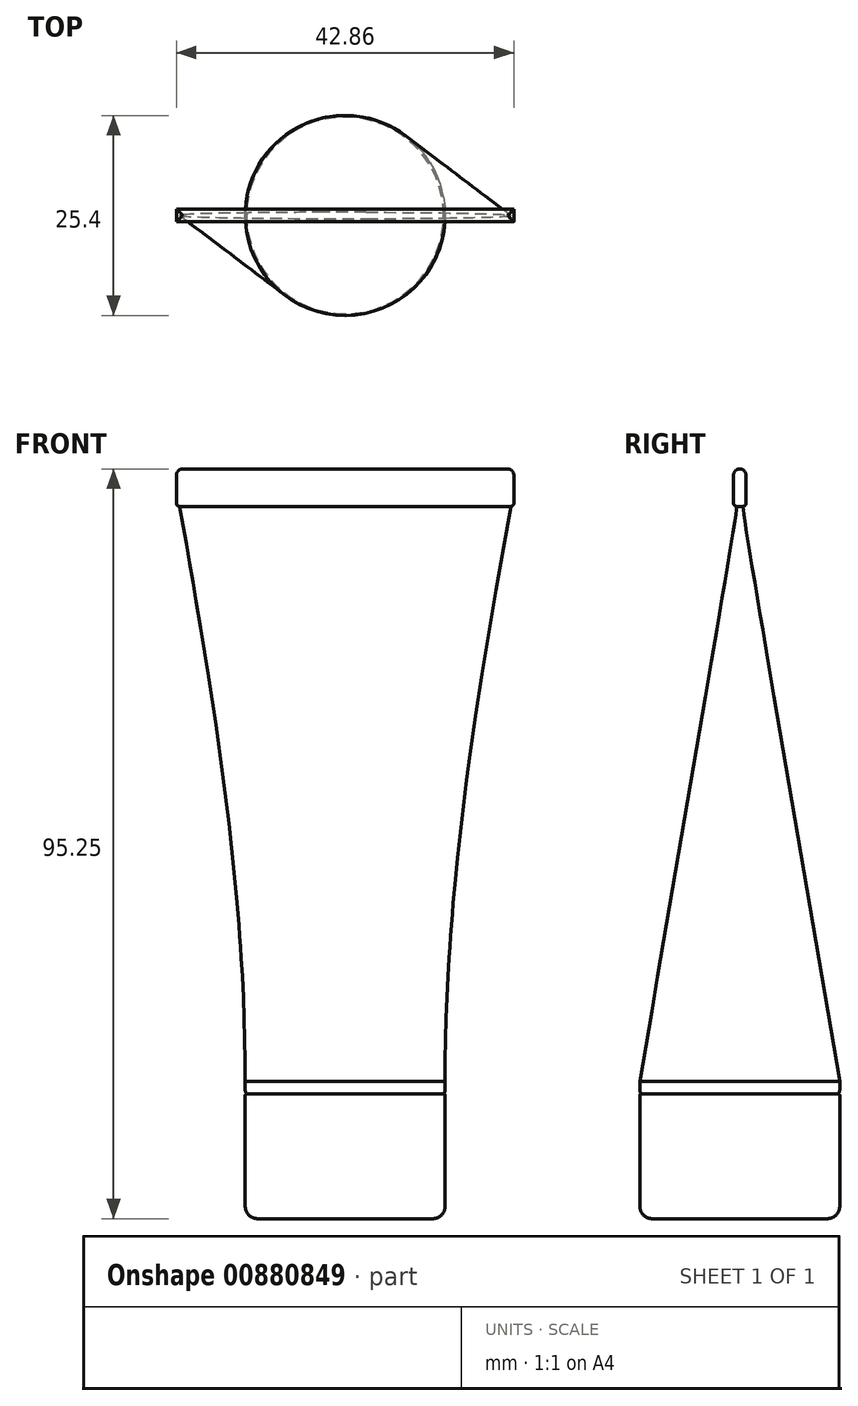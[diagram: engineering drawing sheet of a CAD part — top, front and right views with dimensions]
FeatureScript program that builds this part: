
annotation { "Feature Type Name" : "Feature", "Feature Type Description" : "" }
export const myFeature = defineFeature(function(context is Context, id is Id, definition is map)
    precondition{}
    {
        {
            var Q0;
            Q0=qCreatedBy(makeId("Front.planeOp"),FACE);
            var sketch = newSketch(context, id + "F0", { "sketchPlane" : qUnion([Q0])});
            skLineSegment(sketch, "E0", {"start": v(0, 0) * mm, "end": v(-11.11, 0) * mm});
            skArc(sketch, "E1", {"start": v(-11.11, 0) * mm, "mid": v(-12.24, 0.46) * mm, "end": v(-12.7, 1.59) * mm});
            skLineSegment(sketch, "E2", {"start": v(-12.7, 1.59) * mm, "end": v(-12.7, 15.63) * mm});
            skLineSegment(sketch, "E3", {"start": v(-12.7, 16.4) * mm, "end": v(-12.7, 17.46) * mm});
            skLineSegment(sketch, "E4", {"start": v(-12.7, 17.46) * mm, "end": v(0, 17.46) * mm});
            skLineSegment(sketch, "E5", {"start": v(0, 17.46) * mm, "end": v(0, 0) * mm});
            skArc(sketch, "E6.filletArc", {"start": v(-12.7, 16.4) * mm, "mid": v(-12.65, 16.12) * mm, "end": v(-12.5, 15.88) * mm});
            skArc(sketch, "E7.filletArc", {"start": v(-12.5, 15.88) * mm, "mid": v(-12.64, 15.79) * mm, "end": v(-12.7, 15.63) * mm});
            skSolve(sketch);
        }
        {
            var Q0;
            Q0=makeQuery(id+"F0.imprint","IMPRINT",FACE,{"disambiguationData":[TD([[makeQuery(id+"F0.imprint","IMPRINT",EDGE,{"derivedFrom":sQuery(id+"F0.wireOp",EDGE,"E0")}),-1.0]])]});
            var Q1;
            Q1=sQuery(id+"F0.wireOp",EDGE,"E5");
            revolve(context, id + "F1", {"surfaceOperationType" : NewSurfaceOperationType.NEW, "entities" : qUnion([Q0]), "axis" : qUnion([Q1]), "revolveType" : RevolveType.FULL});
        }
        {
            var Q0;
            Q0=qCreatedBy(makeId("Top.planeOp"),FACE);
            cPlane(context, id + "F2", {"entities" : qUnion([Q0]), "cplaneType" : CPlaneType.OFFSET, "offset" : 95.25 * mm, "width" : 152.4 * mm, "height" : 152.4 * mm});
        }
        {
            var Q0;
            Q0=qCreatedBy(id+"F2.planeOp",FACE);
            var sketch = newSketch(context, id + "F3", { "sketchPlane" : qUnion([Q0])});
            skLineSegment(sketch, "E8.bottom", {"start": v(21.43, 0.8) * mm, "end": v(-21.43, 0.8) * mm});
            skLineSegment(sketch, "E8.top", {"start": v(21.43, -0.8) * mm, "end": v(-21.43, -0.8) * mm});
            skLineSegment(sketch, "E8.left", {"start": v(21.43, 0.8) * mm, "end": v(21.43, -0.8) * mm});
            skLineSegment(sketch, "E8.right", {"start": v(-21.43, 0.8) * mm, "end": v(-21.43, -0.8) * mm});
            skPoint(sketch, "E8.middle", {"position": v(0, 0) * mm});
            skSolve(sketch);
        }
        {
            var Q0;
            Q0 = qSketchRegion(id + "F3", true);
            extrude(context, id + "F4", {"entities" : qUnion([Q0]), "oppositeDirection" : true, "depth" : 4.76 * mm, "offsetDistance" : 25.4 * mm});
        }
        {
            var Q0;
            Q0=makeQuery(id+"F4.opExtrude","CAP_FACE",FACE,{"disambiguationData":[OSD([sQuery(id+"F3.wireOp",EDGE,"E8.bottom"),sQuery(id+"F3.wireOp",EDGE,"E8.top"),sQuery(id+"F3.wireOp",EDGE,"E8.left"),sQuery(id+"F3.wireOp",EDGE,"E8.right")])],"isStart":true});
            fillet(context, id + "F5", {"entities" : qUnion([Q0]), "radius" : 0.8 * mm, "tangentPropagation" : true, "allowEdgeOverflow" : false});
        }
        {
            var Q0;
            Q0=makeQuery(id+"F4.opExtrude","CAP_FACE",FACE,{"disambiguationData":[OSD([sQuery(id+"F3.wireOp",EDGE,"E8.bottom"),sQuery(id+"F3.wireOp",EDGE,"E8.top"),sQuery(id+"F3.wireOp",EDGE,"E8.left"),sQuery(id+"F3.wireOp",EDGE,"E8.right")])],"isStart":false});
            fillet(context, id + "F6", {"entities" : qUnion([Q0]), "radius" : 0.4 * mm, "tangentPropagation" : true, "allowEdgeOverflow" : false});
        }
        {
            var Q0;
            Q0=makeQuery(id+"F4.opExtrude","CAP_FACE",FACE,{"disambiguationData":[OSD([sQuery(id+"F3.wireOp",EDGE,"E8.bottom"),sQuery(id+"F3.wireOp",EDGE,"E8.top"),sQuery(id+"F3.wireOp",EDGE,"E8.left"),sQuery(id+"F3.wireOp",EDGE,"E8.right")])],"isStart":false});
            var sketch = newSketch(context, id + "F7", { "sketchPlane" : qUnion([Q0])});
            skEllipse(sketch, "E9", {"center": v(0, 0) * mm, "majorRadius": 21.04 * mm, "minorRadius": 0.4 * mm, "majorAxis": v(-1, 0)});
            skSolve(sketch);
        }
        {
            var Q0;
            Q0=makeQuery(id+"F1.opRevolve","SWEPT_FACE",FACE,{"disambiguationData":[OSD([sQuery(id+"F0.wireOp",EDGE,"E4")])]});
            var sketch = newSketch(context, id + "F8", { "sketchPlane" : qUnion([Q0])});
            skCircle(sketch, "E10", {"center": v(0, 0) * mm, "radius": 12.7 * mm});
            skSolve(sketch);
        }
        {
            var Q1;
            Q1 = qSketchRegion(id + "F8", true);
            var Q2;
            Q2 = qSketchRegion(id + "F7", true);
            loft(context, id + "F9", {"operationType" : NewBodyOperationType.ADD, "sheetProfilesArray" : [{ "sheetProfileEntities" : qUnion([Q1]) }, { "sheetProfileEntities" : qUnion([Q2]) }]});
        }
    });
